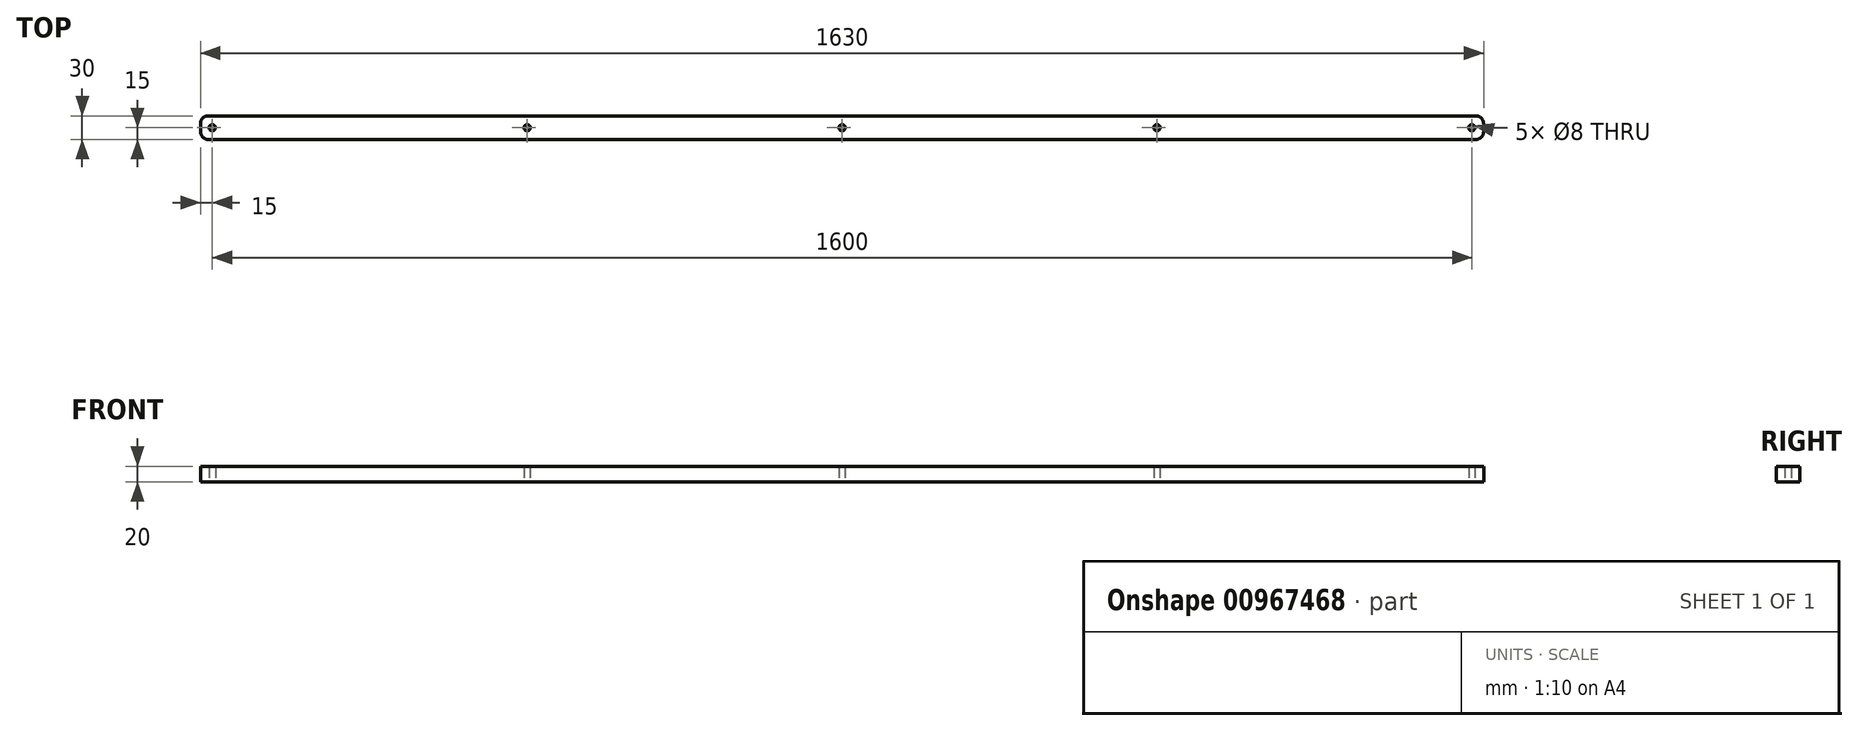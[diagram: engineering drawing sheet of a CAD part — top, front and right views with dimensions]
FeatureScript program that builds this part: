
annotation { "Feature Type Name" : "Feature", "Feature Type Description" : "" }
export const myFeature = defineFeature(function(context is Context, id is Id, definition is map)
    precondition{}
    {
        {
            var Q0;
            Q0=qCreatedBy(makeId("Top.planeOp"),FACE);
            var sketch = newSketch(context, id + "F0", { "sketchPlane" : qUnion([Q0])});
            skLineSegment(sketch, "E0.bottom", {"start": v(815, -15) * mm, "end": v(-815, -15) * mm});
            skLineSegment(sketch, "E0.top", {"start": v(815, 15) * mm, "end": v(-815, 15) * mm});
            skLineSegment(sketch, "E0.left", {"start": v(815, -15) * mm, "end": v(815, 15) * mm});
            skLineSegment(sketch, "E0.right", {"start": v(-815, -15) * mm, "end": v(-815, 15) * mm});
            skPoint(sketch, "E0.middle", {"position": v(0, 0) * mm});
            skCircle(sketch, "E1", {"center": v(-800, 0) * mm, "radius": 4 * mm});
            skPoint(sketch, "E1.centerSnap0", {"position": v(-815, 0) * mm});
            skCircle(sketch, "E2.1.0.0", {"center": v(-400, 0) * mm, "radius": 4 * mm});
            skCircle(sketch, "E2.2.0.0", {"center": v(0, 0) * mm, "radius": 4 * mm});
            skCircle(sketch, "E2.3.0.0", {"center": v(400, 0) * mm, "radius": 4 * mm});
            skLineSegment(sketch, "E2.direction1", {"start": v(-800, 0) * mm, "end": v(-400, 0) * mm, "construction": true});
            skCircle(sketch, "E3.0.4.0", {"center": v(800, 0) * mm, "radius": 4 * mm});
            skSolve(sketch);
        }
        {
            var Q0;
            Q0=makeQuery(id+"F0.imprint","IMPRINT",FACE,{"disambiguationData":[TD([[makeQuery(id+"F0.imprint","IMPRINT",EDGE,{"derivedFrom":sQuery(id+"F0.wireOp",EDGE,"E0.bottom")}),-1.0]])]});
            extrude(context, id + "F1", {"entities" : qUnion([Q0]), "depth" : 20 * mm, "offsetDistance" : 25 * mm});
        }
        {
            var Q0;
            Q0=makeQuery(id+"F1.opExtrude","SWEPT_EDGE",EDGE,{"disambiguationData":[OSD([sQuery(id+"F0.wireOp",EDGE,"E0.top"),sQuery(id+"F0.wireOp",EDGE,"E0.right")])]});
            var Q1;
            Q1=makeQuery(id+"F1.opExtrude","SWEPT_EDGE",EDGE,{"disambiguationData":[OSD([sQuery(id+"F0.wireOp",EDGE,"E0.bottom"),sQuery(id+"F0.wireOp",EDGE,"E0.right")])]});
            var Q2;
            Q2=makeQuery(id+"F1.opExtrude","SWEPT_EDGE",EDGE,{"disambiguationData":[OSD([sQuery(id+"F0.wireOp",EDGE,"E0.top"),sQuery(id+"F0.wireOp",EDGE,"E0.left")])]});
            var Q3;
            Q3=makeQuery(id+"F1.opExtrude","SWEPT_EDGE",EDGE,{"disambiguationData":[OSD([sQuery(id+"F0.wireOp",EDGE,"E0.bottom"),sQuery(id+"F0.wireOp",EDGE,"E0.left")])]});
            fillet(context, id + "F2", {"entities" : qUnion([Q0, Q1, Q2, Q3]), "radius" : 10 * mm, "tangentPropagation" : true, "allowEdgeOverflow" : false});
        }
    });
